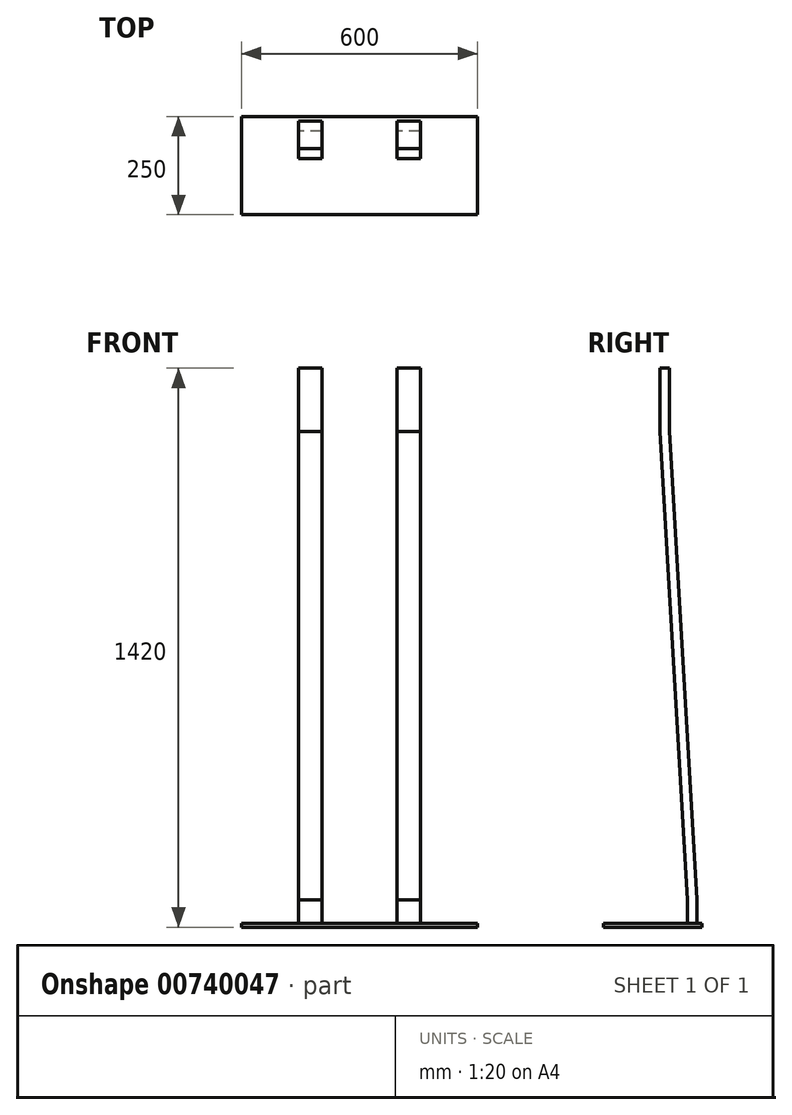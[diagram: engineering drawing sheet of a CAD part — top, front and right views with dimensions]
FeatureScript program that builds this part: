
annotation { "Feature Type Name" : "Feature", "Feature Type Description" : "" }
export const myFeature = defineFeature(function(context is Context, id is Id, definition is map)
    precondition{}
    {
        {
            var Q0;
            Q0=qCreatedBy(makeId("Top.planeOp"),FACE);
            var sketch = newSketch(context, id + "F0", { "sketchPlane" : qUnion([Q0])});
            skLineSegment(sketch, "E0.bottom", {"start": v(-300, 125) * mm, "end": v(300, 125) * mm});
            skLineSegment(sketch, "E0.top", {"start": v(-300, -125) * mm, "end": v(300, -125) * mm});
            skLineSegment(sketch, "E0.left", {"start": v(-300, 125) * mm, "end": v(-300, -125) * mm});
            skLineSegment(sketch, "E0.right", {"start": v(300, 125) * mm, "end": v(300, -125) * mm});
            skPoint(sketch, "E0.middle", {"position": v(0, 0) * mm});
            skSolve(sketch);
        }
        {
            var Q0;
            Q0=makeQuery(id+"F0.imprint","IMPRINT",FACE,{"disambiguationData":[TD([[makeQuery(id+"F0.imprint","IMPRINT",EDGE,{"derivedFrom":sQuery(id+"F0.wireOp",EDGE,"E0.bottom")}),-1.0]])]});
            var sketch = newSketch(context, id + "F1", { "sketchPlane" : qUnion([Q0])});
            skLineSegment(sketch, "E1.bottom", {"start": v(-95, 87.5) * mm, "end": v(-155, 87.5) * mm});
            skLineSegment(sketch, "E1.top", {"start": v(-95, 112.5) * mm, "end": v(-155, 112.5) * mm});
            skLineSegment(sketch, "E1.left", {"start": v(-95, 87.5) * mm, "end": v(-95, 112.5) * mm});
            skLineSegment(sketch, "E1.right", {"start": v(-155, 87.5) * mm, "end": v(-155, 112.5) * mm});
            skPoint(sketch, "E1.middle", {"position": v(-125, 100) * mm});
            skLineSegment(sketch, "E2.bottom", {"start": v(155, 87.5) * mm, "end": v(95, 87.5) * mm});
            skLineSegment(sketch, "E2.top", {"start": v(155, 112.5) * mm, "end": v(95, 112.5) * mm});
            skLineSegment(sketch, "E2.left", {"start": v(155, 87.5) * mm, "end": v(155, 112.5) * mm});
            skLineSegment(sketch, "E2.right", {"start": v(95, 87.5) * mm, "end": v(95, 112.5) * mm});
            skPoint(sketch, "E2.middle", {"position": v(125, 100) * mm});
            skLineSegment(sketch, "E3.0", {"start": v(-300, 125) * mm, "end": v(-300, -125) * mm});
            skLineSegment(sketch, "E4.0", {"start": v(300, 125) * mm, "end": v(300, -125) * mm});
            skLineSegment(sketch, "E5", {"start": v(-125, 100) * mm, "end": v(-300, 100) * mm});
            skLineSegment(sketch, "E6", {"start": v(125, 100) * mm, "end": v(300, 100) * mm});
            skSolve(sketch);
        }
        {
            var Q0;
            Q0=qCreatedBy(makeId("Right.planeOp"),FACE);
            var sketch = newSketch(context, id + "F2", { "sketchPlane" : qUnion([Q0])});
            skPoint(sketch, "E7.0", {"position": v(100, 0) * mm});
            skLineSegment(sketch, "E8", {"start": v(100, 0) * mm, "end": v(100, 60) * mm});
            skLineSegment(sketch, "E9", {"start": v(100, 60) * mm, "end": v(30, 1250) * mm});
            skLineSegment(sketch, "E10", {"start": v(30, 1250) * mm, "end": v(30, 1410) * mm});
            skSolve(sketch);
        }
        {
            var Q0;
            Q0 = qSketchRegion(id + "F2", true);
            var Q1;
            Q1=makeQuery(id+"F0.imprint","IMPRINT",FACE,{"disambiguationData":[TD([[makeQuery(id+"F0.imprint","IMPRINT",EDGE,{"derivedFrom":sQuery(id+"F0.wireOp",EDGE,"E0.bottom")}),-1.0]])]});
            extrude(context, id + "F3", {"entities" : qUnion([Q0, Q1]), "depth" : -10 * mm, "offsetDistance" : 25 * mm});
        }
        {
            var Q0;
            {var subQ3=sQuery(id+"F1.wireOp",EDGE,"E2.bottom");Q0=makeQuery(id+"F1.imprint","IMPRINT",FACE,{"disambiguationData":[TD([[makeQuery(id+"F1.imprint","IMPRINT",EDGE,{"derivedFrom":subQ3}),-1.0]])]});}
            var Q1;
            {var subQ1=sQuery(id+"F1.wireOp",EDGE,"E1.bottom");Q1=makeQuery(id+"F1.imprint","IMPRINT",FACE,{"disambiguationData":[TD([[makeQuery(id+"F1.imprint","IMPRINT",EDGE,{"derivedFrom":subQ1}),-1.0]])]});}
            var Q2;
            Q2=sQuery(id+"F2.wireOp",EDGE,"E8");
            var Q3;
            Q3=sQuery(id+"F2.wireOp",EDGE,"E9");
            var Q4;
            Q4=sQuery(id+"F2.wireOp",EDGE,"E10");
            sweep(context, id + "F4", {"profiles" : qUnion([Q0, Q1]), "path" : qUnion([Q2, Q3, Q4])});
        }
    });
